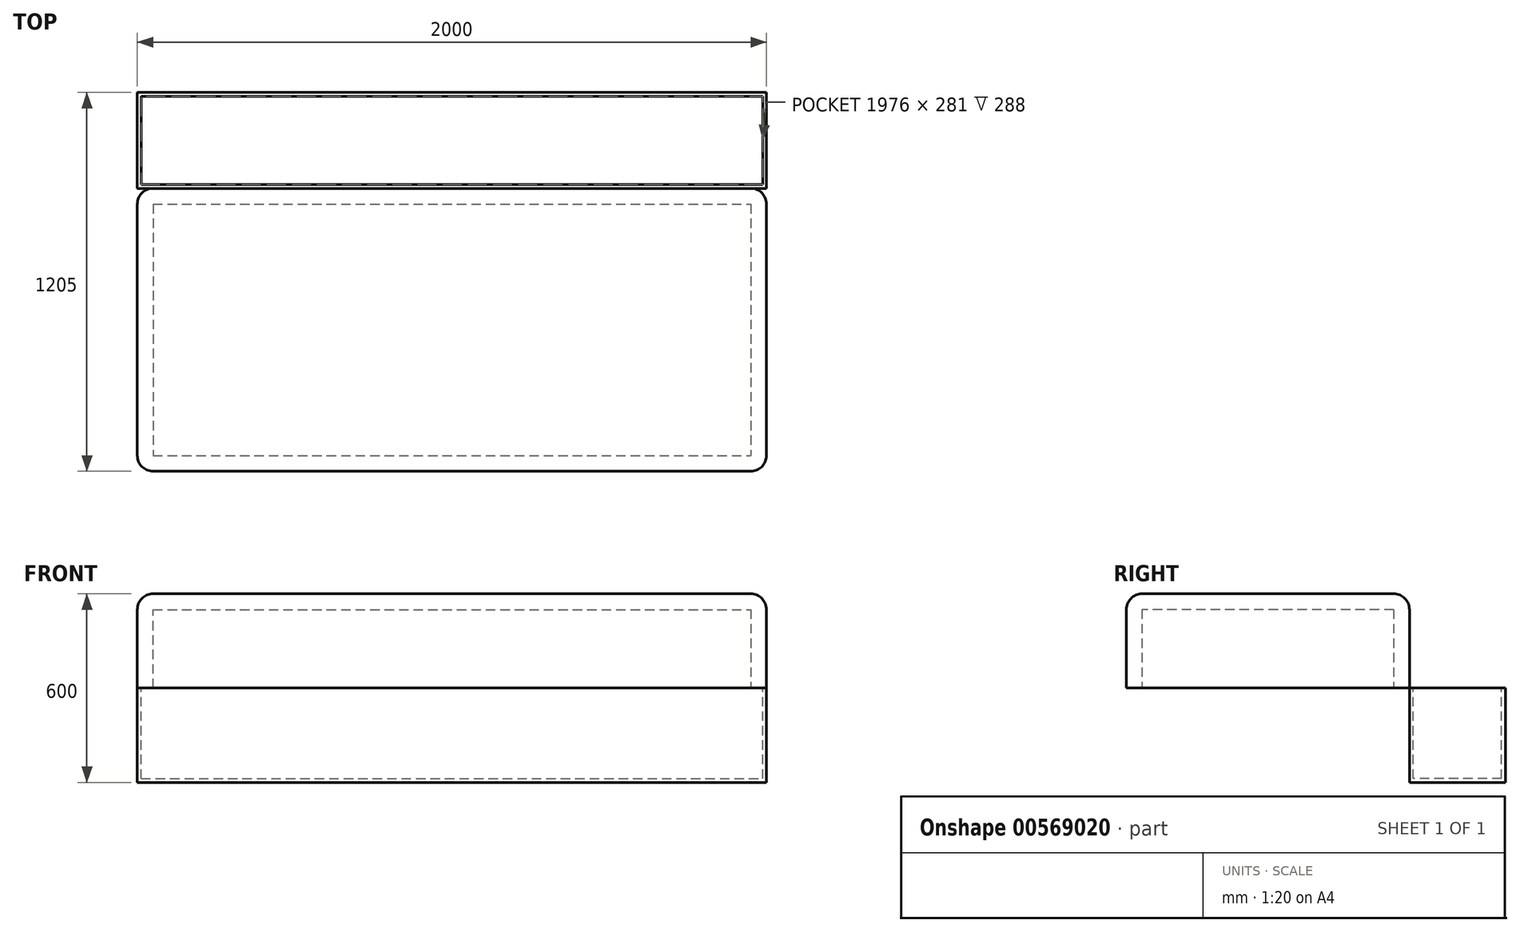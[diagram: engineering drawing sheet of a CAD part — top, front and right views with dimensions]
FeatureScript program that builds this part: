
annotation { "Feature Type Name" : "Feature", "Feature Type Description" : "" }
export const myFeature = defineFeature(function(context is Context, id is Id, definition is map)
    precondition{}
    {
        {
            var Q0;
            Q0=qCreatedBy(makeId("Top.planeOp"),FACE);
            var sketch = newSketch(context, id + "F0", { "sketchPlane" : qUnion([Q0])});
            skLineSegment(sketch, "E0.bottom", {"start": v(-1167.82, 0) * mm, "end": v(832.18, 0) * mm});
            skLineSegment(sketch, "E0.top", {"start": v(-1167.82, -900) * mm, "end": v(832.18, -900) * mm});
            skLineSegment(sketch, "E0.left", {"start": v(-1167.82, 0) * mm, "end": v(-1167.82, -900) * mm});
            skLineSegment(sketch, "E0.right", {"start": v(832.18, 0) * mm, "end": v(832.18, -900) * mm});
            skSolve(sketch);
        }
        {
            var Q0;
            Q0=makeQuery(id+"F0.imprint","IMPRINT",FACE,{"disambiguationData":[TD([[makeQuery(id+"F0.imprint","IMPRINT",EDGE,{"derivedFrom":sQuery(id+"F0.wireOp",EDGE,"E0.bottom")}),-1.0]])]});
            extrude(context, id + "F1", {"entities" : qUnion([Q0]), "depth" : 300 * mm, "offsetDistance" : 25 * mm});
        }
        {
            var Q0;
            Q0=makeQuery(id+"F1.opExtrude","CAP_EDGE",EDGE,{"disambiguationData":[OSD([sQuery(id+"F0.wireOp",EDGE,"E0.top")])],"isStart":false});
            var Q1;
            Q1=makeQuery(id+"F1.opExtrude","CAP_EDGE",EDGE,{"disambiguationData":[OSD([sQuery(id+"F0.wireOp",EDGE,"E0.right")])],"isStart":false});
            var Q2;
            Q2=makeQuery(id+"F1.opExtrude","CAP_EDGE",EDGE,{"disambiguationData":[OSD([sQuery(id+"F0.wireOp",EDGE,"E0.bottom")])],"isStart":false});
            var Q3;
            Q3=makeQuery(id+"F1.opExtrude","CAP_EDGE",EDGE,{"disambiguationData":[OSD([sQuery(id+"F0.wireOp",EDGE,"E0.left")])],"isStart":false});
            var Q4;
            Q4=makeQuery(id+"F1.opExtrude","SWEPT_EDGE",EDGE,{"disambiguationData":[OSD([sQuery(id+"F0.wireOp",EDGE,"E0.top"),sQuery(id+"F0.wireOp",EDGE,"E0.left")])]});
            var Q5;
            Q5=makeQuery(id+"F1.opExtrude","SWEPT_EDGE",EDGE,{"disambiguationData":[OSD([sQuery(id+"F0.wireOp",EDGE,"E0.top"),sQuery(id+"F0.wireOp",EDGE,"E0.right")])]});
            var Q6;
            Q6=makeQuery(id+"F1.opExtrude","SWEPT_EDGE",EDGE,{"disambiguationData":[OSD([sQuery(id+"F0.wireOp",EDGE,"E0.bottom"),sQuery(id+"F0.wireOp",EDGE,"E0.right")])]});
            var Q7;
            Q7=makeQuery(id+"F1.opExtrude","SWEPT_EDGE",EDGE,{"disambiguationData":[OSD([sQuery(id+"F0.wireOp",EDGE,"E0.bottom"),sQuery(id+"F0.wireOp",EDGE,"E0.left")])]});
            fillet(context, id + "F2", {"entities" : qUnion([Q0, Q1, Q2, Q3, Q4, Q5, Q6, Q7]), "radius" : 50 * mm, "tangentPropagation" : true, "allowEdgeOverflow" : false});
        }
        {
            var Q0;
            Q0=makeQuery(id+"F1.opExtrude","CAP_FACE",FACE,{"disambiguationData":[OSD([sQuery(id+"F0.wireOp",EDGE,"E0.bottom"),sQuery(id+"F0.wireOp",EDGE,"E0.top"),sQuery(id+"F0.wireOp",EDGE,"E0.left"),sQuery(id+"F0.wireOp",EDGE,"E0.right")])],"isStart":true});
            shell(context, id + "F3", {"entities" : qUnion([Q0]), "thickness" : 50 * mm});
        }
        {
            var Q0;
            Q0=makeQuery(id+"F1.opExtrude","CAP_FACE",FACE,{"disambiguationData":[OSD([sQuery(id+"F0.wireOp",EDGE,"E0.bottom"),sQuery(id+"F0.wireOp",EDGE,"E0.top"),sQuery(id+"F0.wireOp",EDGE,"E0.left"),sQuery(id+"F0.wireOp",EDGE,"E0.right")])],"isStart":true});
            var sketch = newSketch(context, id + "F4", { "sketchPlane" : qUnion([Q0])});
            skLineSegment(sketch, "E1.0", {"start": v(-1117.82, 0) * mm, "end": v(782.18, 0) * mm});
            skLineSegment(sketch, "E2", {"start": v(832.18, 0) * mm, "end": v(832.18, -305) * mm});
            skLineSegment(sketch, "E3", {"start": v(832.18, -305) * mm, "end": v(-1167.82, -305) * mm});
            skLineSegment(sketch, "E4", {"start": v(-1167.82, -305) * mm, "end": v(-1167.82, 0) * mm});
            skLineSegment(sketch, "E5", {"start": v(-1167.82, 0) * mm, "end": v(-1117.82, 0) * mm});
            skLineSegment(sketch, "E6", {"start": v(832.18, 0) * mm, "end": v(782.18, 0) * mm});
            skSolve(sketch);
        }
        {
            var Q0;
            Q0=makeQuery(id+"F4.imprint","IMPRINT",FACE,{"disambiguationData":[TD([[makeQuery(id+"F4.imprint","IMPRINT",EDGE,{"derivedFrom":sQuery(id+"F4.wireOp",EDGE,"E1.0")}),-1.0]])]});
            extrude(context, id + "F5", {"entities" : qUnion([Q0]), "depth" : 300 * mm, "offsetDistance" : 25 * mm});
        }
        {
            var Q0;
            Q0=makeQuery(id+"F5.opExtrude","CAP_FACE",FACE,{"disambiguationData":[OSD([sQuery(id+"F4.wireOp",EDGE,"E1.0"),sQuery(id+"F4.wireOp",EDGE,"E2"),sQuery(id+"F4.wireOp",EDGE,"E3"),sQuery(id+"F4.wireOp",EDGE,"E4"),sQuery(id+"F4.wireOp",EDGE,"E5"),sQuery(id+"F4.wireOp",EDGE,"E6")])],"isStart":true});
            shell(context, id + "F6", {"entities" : qUnion([Q0]), "thickness" : 12 * mm});
        }
    });
